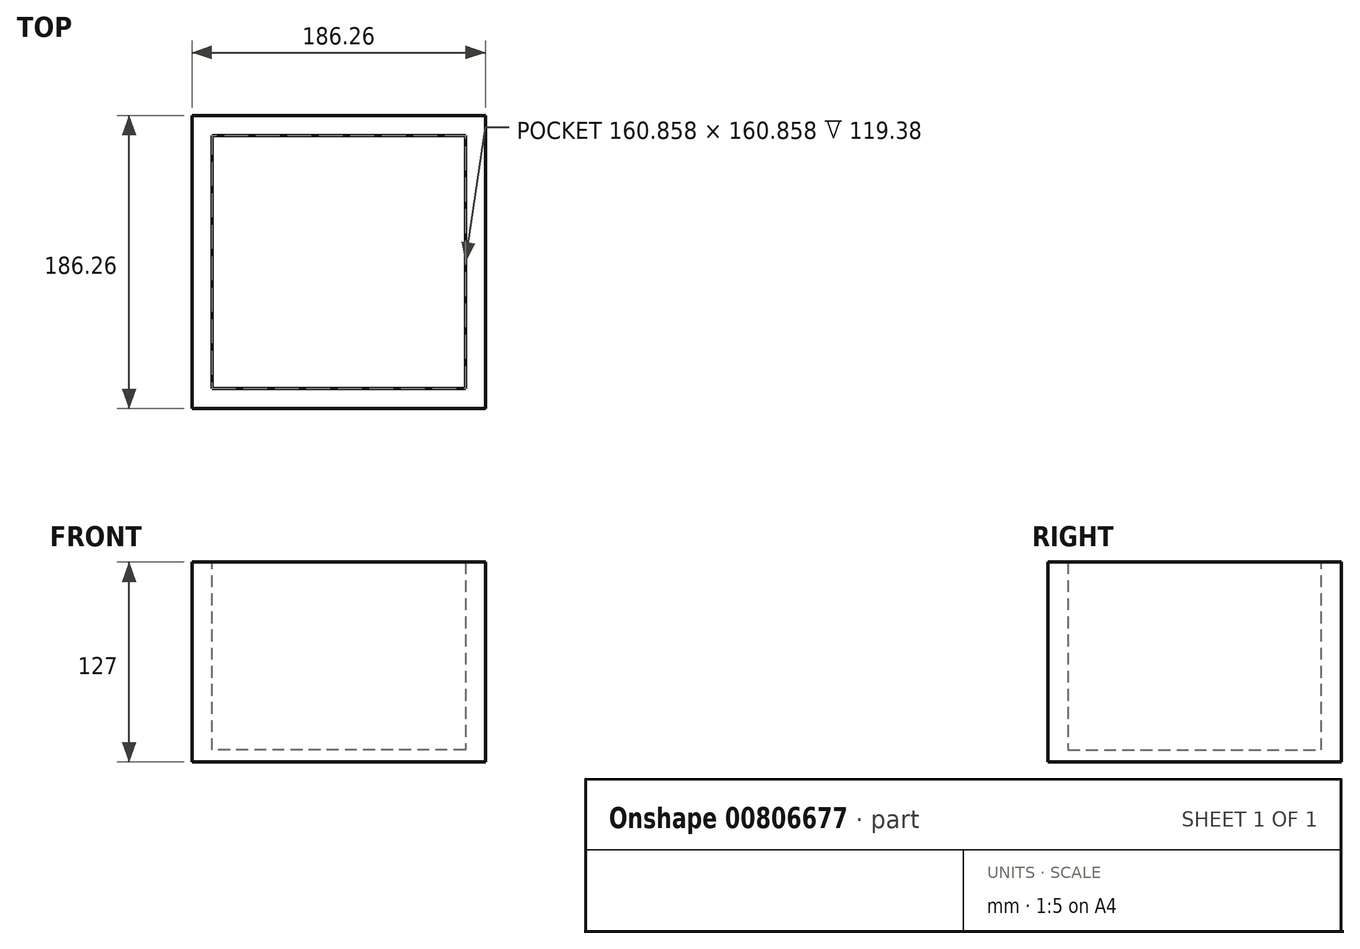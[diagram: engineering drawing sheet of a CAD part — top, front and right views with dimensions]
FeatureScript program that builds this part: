
annotation { "Feature Type Name" : "Feature", "Feature Type Description" : "" }
export const myFeature = defineFeature(function(context is Context, id is Id, definition is map)
    precondition{}
    {
        {
            var Q0;
            Q0=qCreatedBy(makeId("Top.planeOp"),FACE);
            var sketch = newSketch(context, id + "F0", { "sketchPlane" : qUnion([Q0])});
            skLineSegment(sketch, "E0.bottom", {"start": v(80.43, -80.43) * mm, "end": v(-80.43, -80.43) * mm});
            skLineSegment(sketch, "E0.top", {"start": v(80.43, 80.43) * mm, "end": v(-80.43, 80.43) * mm});
            skLineSegment(sketch, "E0.left", {"start": v(80.43, -80.43) * mm, "end": v(80.43, 80.43) * mm});
            skLineSegment(sketch, "E0.right", {"start": v(-80.43, -80.43) * mm, "end": v(-80.43, 80.43) * mm});
            skPoint(sketch, "E0.middle", {"position": v(0, 0) * mm});
            skSolve(sketch);
        }
        {
            var Q0;
            Q0 = qSketchRegion(id + "F0", true);
            var Q1;
            Q1=makeQuery(id+"F0.imprint","IMPRINT",FACE,{"disambiguationData":[TD([[makeQuery(id+"F0.imprint","IMPRINT",EDGE,{"derivedFrom":sQuery(id+"F0.wireOp",EDGE,"E0.bottom")}),-1.0]])]});
            extrude(context, id + "F1", {"entities" : qUnion([Q0, Q1]), "depth" : 7.62 * mm, "offsetDistance" : 25.4 * mm});
        }
        {
            var Q0;
            Q0=qCreatedBy(makeId("Top.planeOp"),FACE);
            var sketch = newSketch(context, id + "F2", { "sketchPlane" : qUnion([Q0])});
            skLineSegment(sketch, "E1.bottom", {"start": v(93.13, -93.13) * mm, "end": v(-93.13, -93.13) * mm});
            skLineSegment(sketch, "E1.top", {"start": v(93.13, 93.13) * mm, "end": v(-93.13, 93.13) * mm});
            skLineSegment(sketch, "E1.left", {"start": v(93.13, -93.13) * mm, "end": v(93.13, 93.13) * mm});
            skLineSegment(sketch, "E1.right", {"start": v(-93.13, -93.13) * mm, "end": v(-93.13, 93.13) * mm});
            skPoint(sketch, "E1.middle", {"position": v(0, 0) * mm});
            skLineSegment(sketch, "E2.bottom", {"start": v(80.43, -80.43) * mm, "end": v(-80.43, -80.43) * mm});
            skLineSegment(sketch, "E2.top", {"start": v(80.43, 80.43) * mm, "end": v(-80.43, 80.43) * mm});
            skLineSegment(sketch, "E2.left", {"start": v(80.43, -80.43) * mm, "end": v(80.43, 80.43) * mm});
            skLineSegment(sketch, "E2.right", {"start": v(-80.43, -80.43) * mm, "end": v(-80.43, 80.43) * mm});
            skSolve(sketch);
        }
        {
            var Q0;
            Q0 = qSketchRegion(id + "F2", true);
            var Q1;
            Q1=makeQuery(id+"F2.imprint","IMPRINT",FACE,{"disambiguationData":[TD([[makeQuery(id+"F2.imprint","IMPRINT",EDGE,{"derivedFrom":sQuery(id+"F2.wireOp",EDGE,"E1.bottom")}),-1.0]])]});
            extrude(context, id + "F3", {"entities" : qUnion([Q0, Q1]), "operationType" : NewBodyOperationType.ADD, "depth" : 127 * mm, "offsetDistance" : 25.4 * mm});
        }
    });
